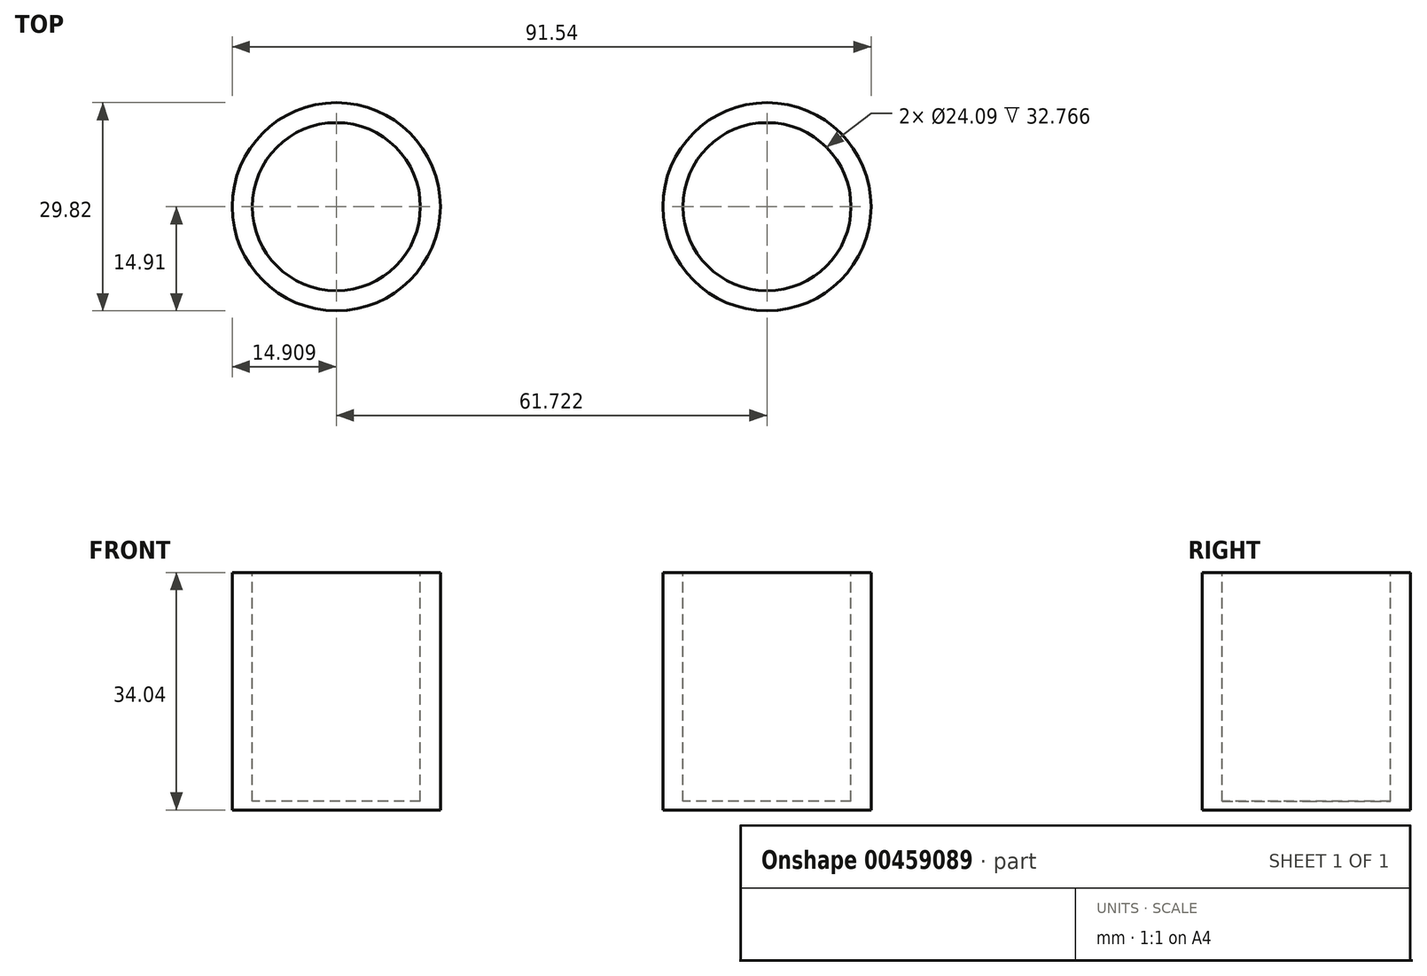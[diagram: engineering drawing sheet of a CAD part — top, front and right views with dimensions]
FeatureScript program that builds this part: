
annotation { "Feature Type Name" : "Feature", "Feature Type Description" : "" }
export const myFeature = defineFeature(function(context is Context, id is Id, definition is map)
    precondition{}
    {
        {
            var Q0;
            Q0=qCreatedBy(makeId("Top.planeOp"),FACE);
            var sketch = newSketch(context, id + "F0", { "sketchPlane" : qUnion([Q0])});
            skCircle(sketch, "E0", {"center": v(-29.01, 0) * mm, "radius": 14.91 * mm});
            skSolve(sketch);
        }
        {
            var Q0;
            Q0=makeQuery(id+"F0.imprint","IMPRINT",FACE,{"disambiguationData":[TD([[makeQuery(id+"F0.imprint","IMPRINT",EDGE,{"derivedFrom":sQuery(id+"F0.wireOp",EDGE,"E0")}),1.0]])]});
            extrude(context, id + "F1", {"entities" : qUnion([Q0]), "oppositeDirection" : true, "depth" : 34.04 * mm});
        }
        {
            var Q0;
            Q0=qCreatedBy(makeId("Top.planeOp"),FACE);
            var sketch = newSketch(context, id + "F2", { "sketchPlane" : qUnion([Q0])});
            skCircle(sketch, "E1", {"center": v(-29.01, 0) * mm, "radius": 12.05 * mm});
            skSolve(sketch);
        }
        {
            var Q0;
            Q0 = qSketchRegion(id + "F2", true);
            var Q1;
            Q1=sQuery(id+"F2.wireOp",EDGE,"E1");
            extrude(context, id + "F3", {"entities" : qUnion([Q0]), "operationType" : NewBodyOperationType.REMOVE, "surfaceEntities" : qUnion([Q1]), "oppositeDirection" : true, "depth" : 32.77 * mm});
        }
        {
            var Q0;
            Q0=makeQuery(id+"F1.opExtrude","SWEPT_BODY",BODY,{"disambiguationData":[OSD([sQuery(id+"F0.wireOp",EDGE,"E0")])]});
            transform(context, id + "F4", {"entities" : qUnion([Q0]), "transformType" : TransformType.TRANSLATION_3D, "dx" : 61.72 * mm, "dy" : 0 * mm, "dz" : 0 * mm, "makeCopy" : true});
        }
    });
